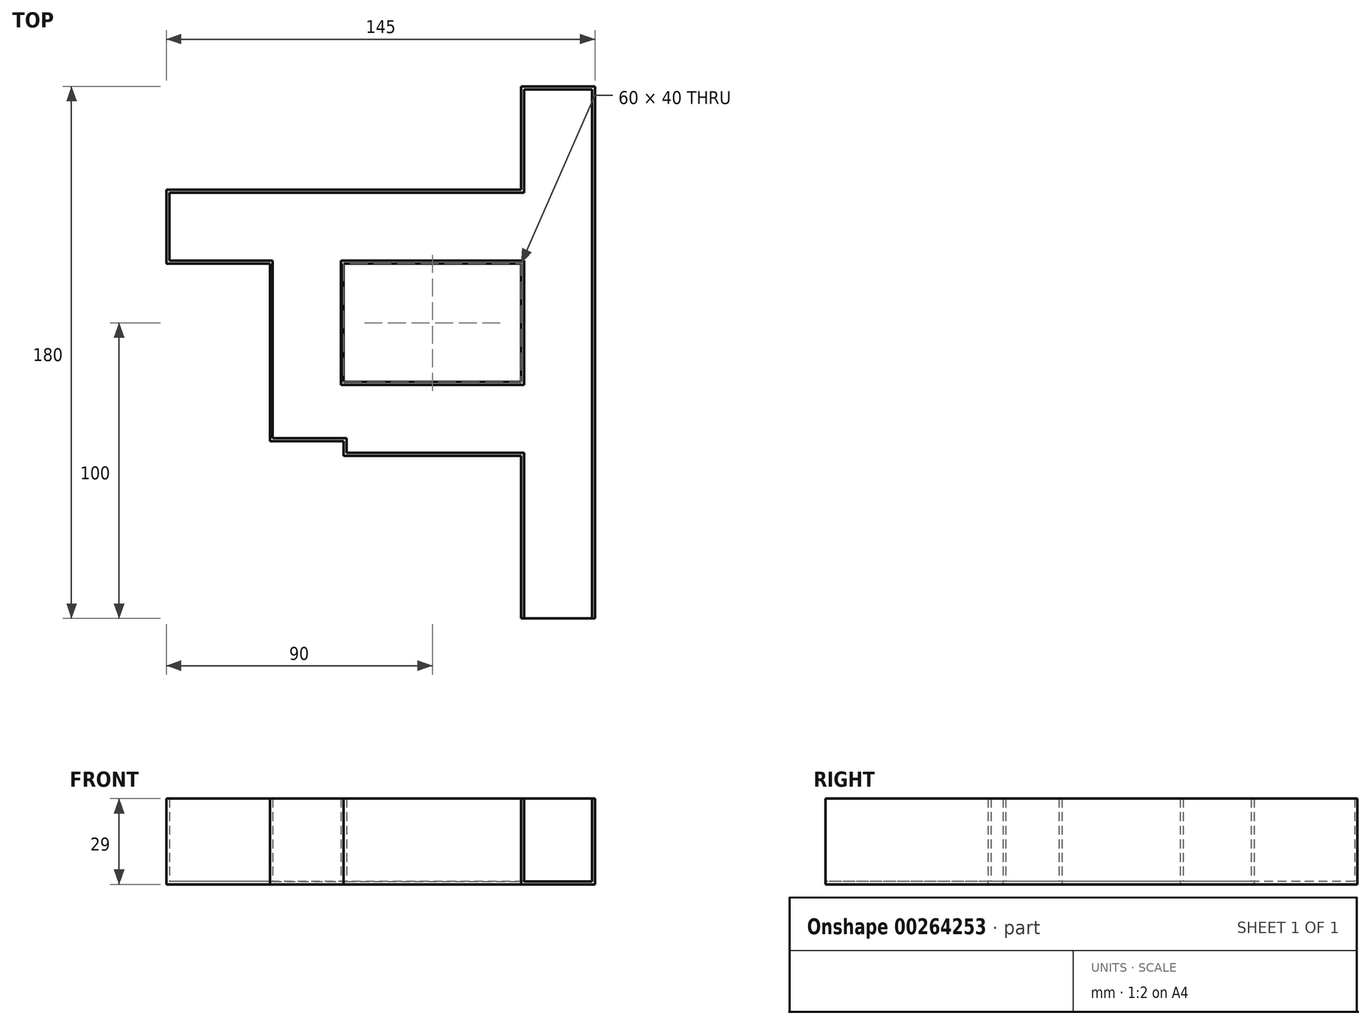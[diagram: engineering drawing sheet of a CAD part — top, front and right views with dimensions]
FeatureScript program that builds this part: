
annotation { "Feature Type Name" : "Feature", "Feature Type Description" : "" }
export const myFeature = defineFeature(function(context is Context, id is Id, definition is map)
    precondition{}
    {
        {
            var Q0;
            Q0=qCreatedBy(makeId("Top.planeOp"),FACE);
            var sketch = newSketch(context, id + "F0", { "sketchPlane" : qUnion([Q0])});
            skLineSegment(sketch, "E0.bottom", {"start": v(0, 0) * mm, "end": v(-25, 0) * mm});
            skLineSegment(sketch, "E0.top", {"start": v(0, -120) * mm, "end": v(-25, -120) * mm});
            skLineSegment(sketch, "E0.left", {"start": v(0, 0) * mm, "end": v(0, -120) * mm});
            skLineSegment(sketch, "E0.right", {"start": v(-25, 0) * mm, "end": v(-25, -120) * mm});
            skLineSegment(sketch, "E1.bottom", {"start": v(-25, -35) * mm, "end": v(-145, -35) * mm});
            skLineSegment(sketch, "E1.top", {"start": v(-25, -60) * mm, "end": v(-145, -60) * mm});
            skLineSegment(sketch, "E1.left", {"start": v(-25, -35) * mm, "end": v(-25, -60) * mm});
            skLineSegment(sketch, "E1.right", {"start": v(-145, -35) * mm, "end": v(-145, -60) * mm});
            skLineSegment(sketch, "E2.bottom", {"start": v(-110, -60) * mm, "end": v(-85, -60) * mm});
            skLineSegment(sketch, "E2.top", {"start": v(-110, -120) * mm, "end": v(-85, -120) * mm});
            skLineSegment(sketch, "E2.left", {"start": v(-110, -60) * mm, "end": v(-110, -120) * mm});
            skLineSegment(sketch, "E2.right", {"start": v(-85, -60) * mm, "end": v(-85, -120) * mm});
            skLineSegment(sketch, "E3.bottom", {"start": v(-25, -120) * mm, "end": v(0, -120) * mm});
            skLineSegment(sketch, "E3.top", {"start": v(-25, -180) * mm, "end": v(0, -180) * mm});
            skLineSegment(sketch, "E3.left", {"start": v(-25, -120) * mm, "end": v(-25, -180) * mm});
            skLineSegment(sketch, "E3.right", {"start": v(0, -120) * mm, "end": v(0, -180) * mm});
            skLineSegment(sketch, "E4.bottom", {"start": v(-85, -100) * mm, "end": v(-25, -100) * mm});
            skLineSegment(sketch, "E4.top", {"start": v(-85, -125) * mm, "end": v(-25, -125) * mm});
            skLineSegment(sketch, "E4.left", {"start": v(-85, -100) * mm, "end": v(-85, -125) * mm});
            skLineSegment(sketch, "E4.right", {"start": v(-25, -100) * mm, "end": v(-25, -125) * mm});
            skSolve(sketch);
        }
        {
            var Q0;
            Q0 = qSketchRegion(id + "F0", true);
            extrude(context, id + "F1", {"entities" : qUnion([Q0]), "depth" : 30 * mm, "offsetDistance" : 25 * mm});
        }
        {
            var Q0;
            Q0=makeQuery(id+"F1.opExtrude","SWEPT_FACE",FACE,{"disambiguationData":[OSD([sQuery(id+"F0.wireOp",EDGE,"E3.top")])]});
            shell(context, id + "F2", {"entities" : qUnion([Q0]), "thickness" : 1 * mm});
        }
        {
            var Q0;
            Q0=makeQuery(id+"F1.opExtrude","CAP_FACE",FACE,{"disambiguationData":[OSD([sQuery(id+"F0.wireOp",EDGE,"E0.bottom"),sQuery(id+"F0.wireOp",EDGE,"E0.left"),sQuery(id+"F0.wireOp",EDGE,"E0.right"),sQuery(id+"F0.wireOp",EDGE,"E1.bottom"),sQuery(id+"F0.wireOp",EDGE,"E1.top"),sQuery(id+"F0.wireOp",EDGE,"E1.right"),sQuery(id+"F0.wireOp",EDGE,"E2.top"),sQuery(id+"F0.wireOp",EDGE,"E2.left"),sQuery(id+"F0.wireOp",EDGE,"E2.right"),sQuery(id+"F0.wireOp",EDGE,"E3.top"),sQuery(id+"F0.wireOp",EDGE,"E3.left"),sQuery(id+"F0.wireOp",EDGE,"E3.right"),sQuery(id+"F0.wireOp",EDGE,"E4.bottom"),sQuery(id+"F0.wireOp",EDGE,"E4.top"),sQuery(id+"F0.wireOp",EDGE,"E4.left")])],"isStart":false});
            extrude(context, id + "F3", {"entities" : qUnion([Q0]), "operationType" : NewBodyOperationType.REMOVE, "oppositeDirection" : true, "depth" : 1 * mm, "offsetDistance" : 25 * mm});
        }
    });
